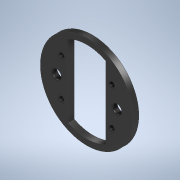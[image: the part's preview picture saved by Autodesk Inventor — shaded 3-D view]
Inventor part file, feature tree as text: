
AUTODESK INVENTOR PART (.ipt)
format: ipt  version: 2020 (Build 240168000, 168)  size: 157,184 bytes
history: native  units: in
note: dims shown in document units (in); Inventor stores cm internally (conversion verified against a paired STEP export)
features: sketch x4, hole x2, revolve x1, extrude x1
ambient origin geometry x8: Origin, YZ Plane, XZ Plane, XY Plane, X Axis, Y Axis, Z Axis, Center Point
bodies: Solid1 (feature_tree)
feature tree (8):
  revolve  "Revolution1"  [1 undecoded]
  extrude  "Extrusion1"  Depth=0.25in
  hole  "Hole1"  [1 undecoded]
  hole  "Hole2"  [1 undecoded]
  sketch  "Sketch1"  dims[d0=1.85in d2=0.125in]
  sketch  "Sketch2"  dims[d3=0.25in d4=1.75in]
  sketch  "Sketch3"  dims[d5=90.0deg d6=3.25in]
  sketch  "Sketch4"  dims[d7=1.5in d8=0.0in d9=0.0in d10=0.0312in d11=2.0in d12=1.5in d13=0.205in d14=0.75in d15=0.375in d16=0.25in d17=0.5635in d18=0.75in d19=0.0in d20=2.4in d21=0.375in d22=0.75in d23=0.51in d24=0.188in d25=0.5635in d26=0.75in d27=0.0in]
note: 3 required parameter values undecoded (feature->parameter linkage not recoverable at this tier; creation-order binding heuristic only, values carry confidence <= 0.55)